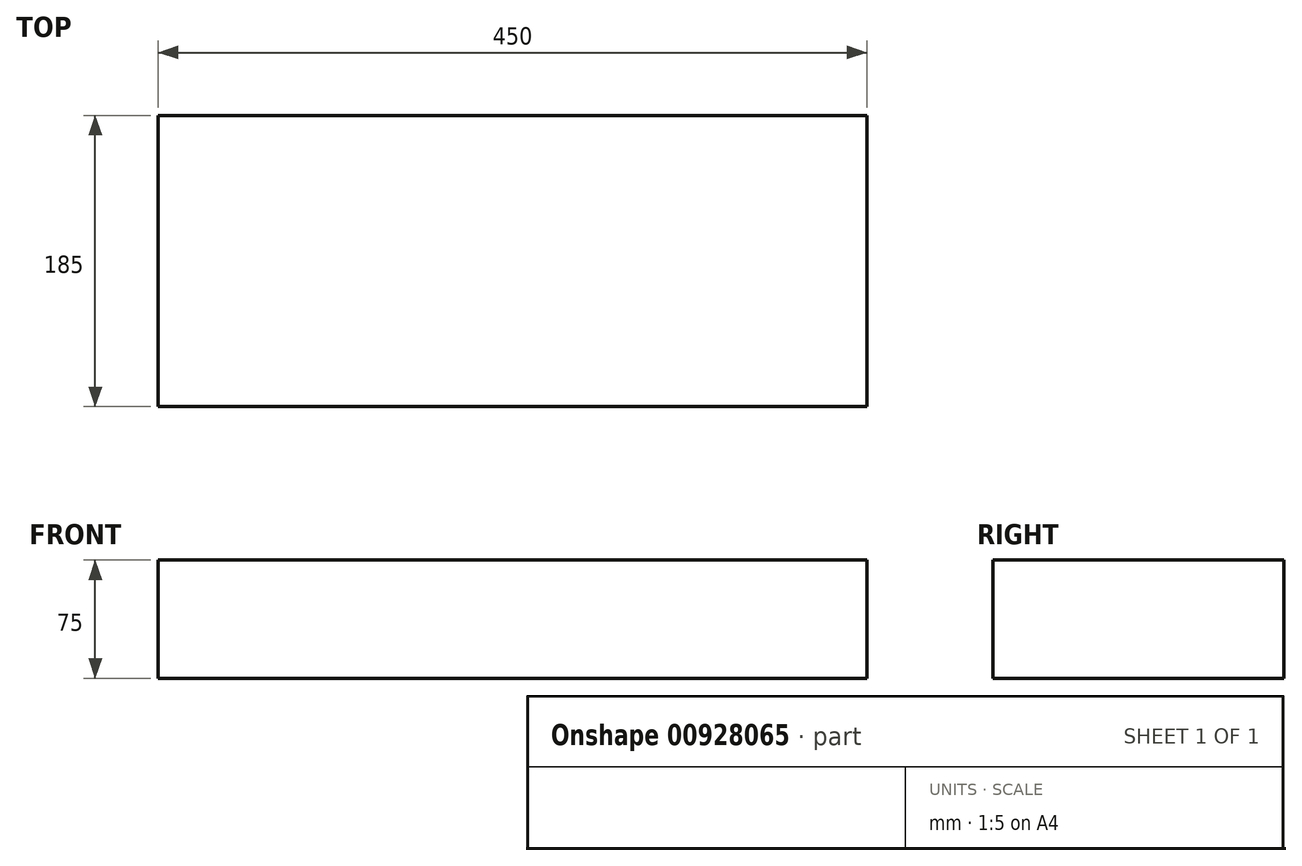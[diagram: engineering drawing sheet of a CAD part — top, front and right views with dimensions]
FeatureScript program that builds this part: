
annotation { "Feature Type Name" : "Feature", "Feature Type Description" : "" }
export const myFeature = defineFeature(function(context is Context, id is Id, definition is map)
    precondition{}
    {
        {
            var Q0;
            Q0=qCreatedBy(makeId("Right.planeOp"),FACE);
            var sketch = newSketch(context, id + "F0", { "sketchPlane" : qUnion([Q0])});
            skLineSegment(sketch, "E0.bottom", {"start": v(-92.72, 32.7) * mm, "end": v(92.28, 32.7) * mm});
            skLineSegment(sketch, "E0.top", {"start": v(-92.72, -42.3) * mm, "end": v(92.28, -42.3) * mm});
            skLineSegment(sketch, "E0.left", {"start": v(-92.72, 32.7) * mm, "end": v(-92.72, -42.3) * mm});
            skLineSegment(sketch, "E0.right", {"start": v(92.28, 32.7) * mm, "end": v(92.28, -42.3) * mm});
            skSolve(sketch);
        }
        {
            var Q0;
            Q0=makeQuery(id+"F0.imprint","IMPRINT",FACE,{"disambiguationData":[TD([[makeQuery(id+"F0.imprint","IMPRINT",EDGE,{"derivedFrom":sQuery(id+"F0.wireOp",EDGE,"E0.bottom")}),-1.0]])]});
            extrude(context, id + "F1", {"entities" : qUnion([Q0]), "depth" : 450 * mm, "offsetDistance" : 25 * mm});
        }
    });
